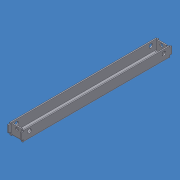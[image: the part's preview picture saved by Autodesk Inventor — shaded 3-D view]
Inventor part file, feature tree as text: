
AUTODESK INVENTOR PART (.ipt)
format: ipt  version: 2015 (Build 190159000, 159)  size: 306,176 bytes
history: native  units: mm
features: other x10, sheet_metal_op x9, sketch x8, plane x1
ambient origin geometry x8: Origin, YZ Plane, XZ Plane, XY Plane, X Axis, Y Axis, Z Axis, Center Point
bodies: Solid1 (feature_tree)
feature tree (28):
  sheet_metal_op  "Face1"
  sheet_metal_op  "Flange1"
  sheet_metal_op  "Flange2"
  plane  "Work Plane1"
  sheet_metal_op  "Flange5"
  sheet_metal_op  "Flange6"
  sketch  "Sketch1"  dims[d2=34.0mm]
  other  "Plate1"
  sketch  "Sketch2"  dims[d3=416.0mm]
  other  "Plate2"
  sheet_metal_op  "Bend1"
  sketch  "Sketch3"  dims[d4=0.001mm]
  other  "Plate3"
  sheet_metal_op  "Bend2"
  other  "FlatPattern"
  sketch  "Sketch7"  dims[d5=-5.0mm d6=-5.0mm]
  sketch  "Sketch8"  dims[d7=0.5mm]
  other  "Plate6"
  sheet_metal_op  "Bend5"
  sketch  "Sketch9"  dims[d8=4.5mm]
  other  "Plate7"
  sheet_metal_op  "Bend6"
  sketch  "Sketch10"  dims[d9=6.0mm]
  sketch  "Sketch11"  dims[d10=0.001mm d11=27.0mm d12=90.0deg d13=0.001mm d14=-5.0mm d15=-5.0mm d16=0.5mm d17=4.5mm d18=6.0mm d19=0.001mm d20=27.0mm d21=90.0deg d22=0.001mm d47=11.0mm d48=11.0mm d49=22.0mm d50=10.0mm d51=22.0mm d52=10.0mm d53=3.0mm d54=0.0mm d55=1.0mm d56=3.0mm d57=3.0mm d58=1.0mm d59=3.0mm d60=3.0mm d61=34.0mm d62=1.0mm d63=0.5mm d64=4.5mm d65=6.0mm d66=0.001mm d67=27.0mm d68=90.0deg d69=0.001mm d70=0.5mm d71=4.5mm d72=6.0mm d73=0.001mm d74=27.0mm d75=90.0deg d76=0.001mm d77=9.0mm d78=13.5mm d79=7.0mm d80=3.0mm d81=0.0mm d82=5.0mm d83=3.0mm d84=5.0mm d85=3.0mm d86=3.0mm d87=0.0mm d0=3.0mm]
  other  "Cut2"
  other  "Cut3"
  other  "Cut4"
  other  "FlatPatternExtrusion2"
